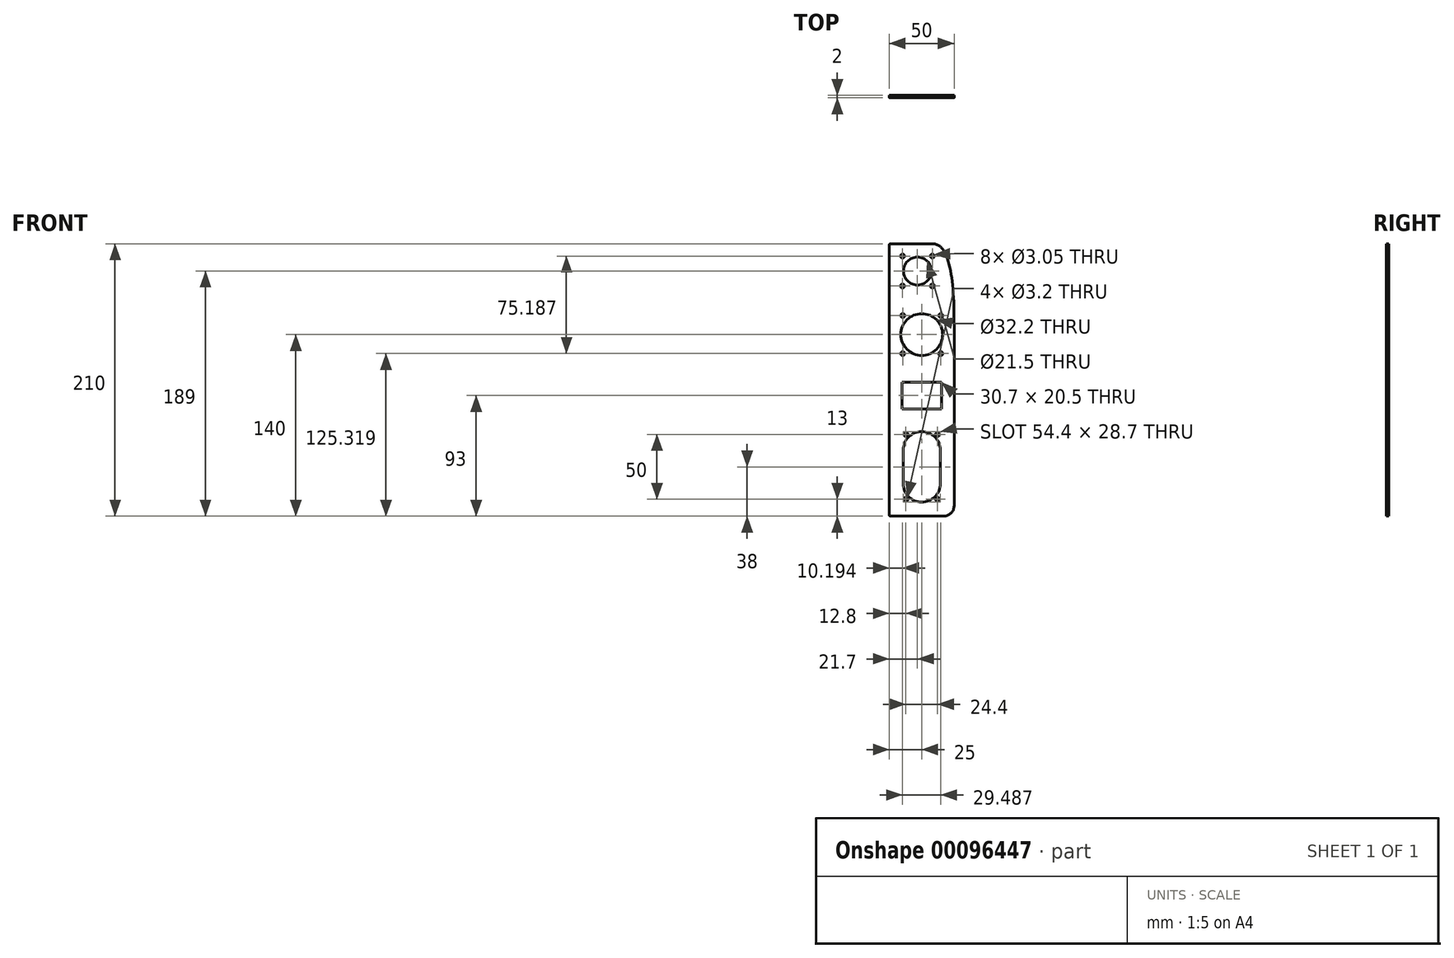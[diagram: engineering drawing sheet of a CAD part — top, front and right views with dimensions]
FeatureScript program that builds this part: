
annotation { "Feature Type Name" : "Feature", "Feature Type Description" : "" }
export const myFeature = defineFeature(function(context is Context, id is Id, definition is map)
    precondition{}
    {
        {
            var Q0;
            Q0=qCreatedBy(makeId("Front.planeOp"),FACE);
            var sketch = newSketch(context, id + "F0", { "sketchPlane" : qUnion([Q0])});
            skLineSegment(sketch, "E0.bottom", {"start": v(1, 0) * mm, "end": v(42, 0) * mm});
            skLineSegment(sketch, "E0.top", {"start": v(1, 210) * mm, "end": v(33.06, 210) * mm});
            skLineSegment(sketch, "E0.left", {"start": v(0, 1) * mm, "end": v(0, 209) * mm});
            skLineSegment(sketch, "E0.right", {"start": v(50, 8) * mm, "end": v(50, 209) * mm});
            skLineSegment(sketch, "E1.bottom", {"start": v(9.65, 103.25) * mm, "end": v(40.35, 103.25) * mm});
            skLineSegment(sketch, "E1.top", {"start": v(9.65, 82.75) * mm, "end": v(40.35, 82.75) * mm});
            skLineSegment(sketch, "E1.left", {"start": v(9.65, 103.25) * mm, "end": v(9.65, 82.75) * mm});
            skLineSegment(sketch, "E1.right", {"start": v(40.35, 103.25) * mm, "end": v(40.35, 82.75) * mm});
            skLineSegment(sketch, "E2", {"start": v(9.65, 93) * mm, "end": v(40.35, 93) * mm, "construction": true});
            skLineSegment(sketch, "E3", {"start": v(25, 103.25) * mm, "end": v(25, 82.75) * mm, "construction": true});
            skArc(sketch, "E4", {"start": v(10.65, 25.15) * mm, "mid": v(25, 10.8) * mm, "end": v(39.35, 25.15) * mm});
            skLineSegment(sketch, "E5", {"start": v(25, 50.85) * mm, "end": v(25, 25.15) * mm, "construction": true});
            skLineSegment(sketch, "E6", {"start": v(10.65, 50.85) * mm, "end": v(10.65, 25.15) * mm});
            skLineSegment(sketch, "E7", {"start": v(39.35, 50.85) * mm, "end": v(39.35, 25.15) * mm});
            skArc(sketch, "E8.trimOffspring", {"start": v(39.35, 50.85) * mm, "mid": v(25, 65.2) * mm, "end": v(10.65, 50.85) * mm});
            skPoint(sketch, "E9", {"position": v(25, 38) * mm});
            skLineSegment(sketch, "E10.bottom", {"start": v(37.2, 63) * mm, "end": v(12.8, 63) * mm, "construction": true});
            skLineSegment(sketch, "E10.top", {"start": v(37.2, 13) * mm, "end": v(12.8, 13) * mm, "construction": true});
            skLineSegment(sketch, "E10.left", {"start": v(37.2, 63) * mm, "end": v(37.2, 13) * mm, "construction": true});
            skLineSegment(sketch, "E10.right", {"start": v(12.8, 63) * mm, "end": v(12.8, 13) * mm, "construction": true});
            skCircle(sketch, "E11", {"center": v(37.2, 63) * mm, "radius": 1.6 * mm});
            skCircle(sketch, "E12", {"center": v(12.8, 63) * mm, "radius": 1.6 * mm});
            skCircle(sketch, "E13", {"center": v(12.8, 13) * mm, "radius": 1.6 * mm});
            skCircle(sketch, "E14", {"center": v(37.2, 13) * mm, "radius": 1.6 * mm});
            skPoint(sketch, "E15.visualSharp", {"position": v(0, 210) * mm});
            skArc(sketch, "E15.filletArc", {"start": v(1, 210) * mm, "mid": v(0.3, 209.7) * mm, "end": v(0, 209) * mm});
            skPoint(sketch, "E16.visualSharp", {"position": v(50, 210) * mm});
            skArc(sketch, "E16.filletArc", {"start": v(50, 209) * mm, "mid": v(49.7, 209.7) * mm, "end": v(49, 210) * mm});
            skPoint(sketch, "E17.visualSharp", {"position": v(50, 0) * mm});
            skPoint(sketch, "E18.visualSharp", {"position": v(0, 0) * mm});
            skArc(sketch, "E18.filletArc", {"start": v(0, 1) * mm, "mid": v(0.3, 0.3) * mm, "end": v(1, 0) * mm});
            skCircle(sketch, "E19", {"center": v(21.7, 189) * mm, "radius": 10.75 * mm});
            skCircle(sketch, "E20", {"center": v(33.2, 200.5) * mm, "radius": 1.52 * mm});
            skCircle(sketch, "E21", {"center": v(25, 140) * mm, "radius": 16.1 * mm});
            skCircle(sketch, "E22", {"center": v(39.68, 154.68) * mm, "radius": 1.52 * mm});
            skLineSegment(sketch, "E23", {"start": v(21.7, 152.5) * mm, "end": v(21.7, 189) * mm, "construction": true});
            skLineSegment(sketch, "E24", {"start": v(25, 140) * mm, "end": v(25, 151.6) * mm, "construction": true});
            skCircle(sketch, "E25.MirrorC", {"center": v(10.32, 154.68) * mm, "radius": 1.52 * mm});
            skCircle(sketch, "E26.MirrorC", {"center": v(39.68, 125.32) * mm, "radius": 1.52 * mm});
            skCircle(sketch, "E27.MirrorC", {"center": v(10.32, 125.32) * mm, "radius": 1.52 * mm});
            skCircle(sketch, "E28.MirrorC", {"center": v(10.2, 200.5) * mm, "radius": 1.52 * mm});
            skLineSegment(sketch, "E29", {"start": v(25, 0) * mm, "end": v(25, 165.66) * mm, "construction": true});
            skCircle(sketch, "E30.MirrorC", {"center": v(33.2, 177.5) * mm, "radius": 1.52 * mm});
            skCircle(sketch, "E31.MirrorC", {"center": v(10.2, 177.5) * mm, "radius": 1.52 * mm});
            skArc(sketch, "E32.filletArc", {"start": v(42, 0) * mm, "mid": v(47.66, 2.34) * mm, "end": v(50, 8) * mm});
            skLineSegment(sketch, "E33", {"start": v(0, 0) * mm, "end": v(50, 0) * mm, "construction": true});
            skFitSpline(sketch, "E34", {"points": [v(38.33, 210) * mm, v(50, 134) * mm], "startDerivative": vector(35.02, -43.11) * mm, "endDerivative": vector(0, -113.63) * mm});
            skArc(sketch, "E35.filletArc", {"start": v(41.79, 204.88) * mm, "mid": v(38.12, 208.63) * mm, "end": v(33.06, 210) * mm});
            skSolve(sketch);
        }
        {
            var Q0;
            Q0=qSketchRegion(id+"F0",true);
            extrude(context, id + "F1", {"entities" : qUnion([Q0]), "depth" : 2 * mm});
        }
    });
